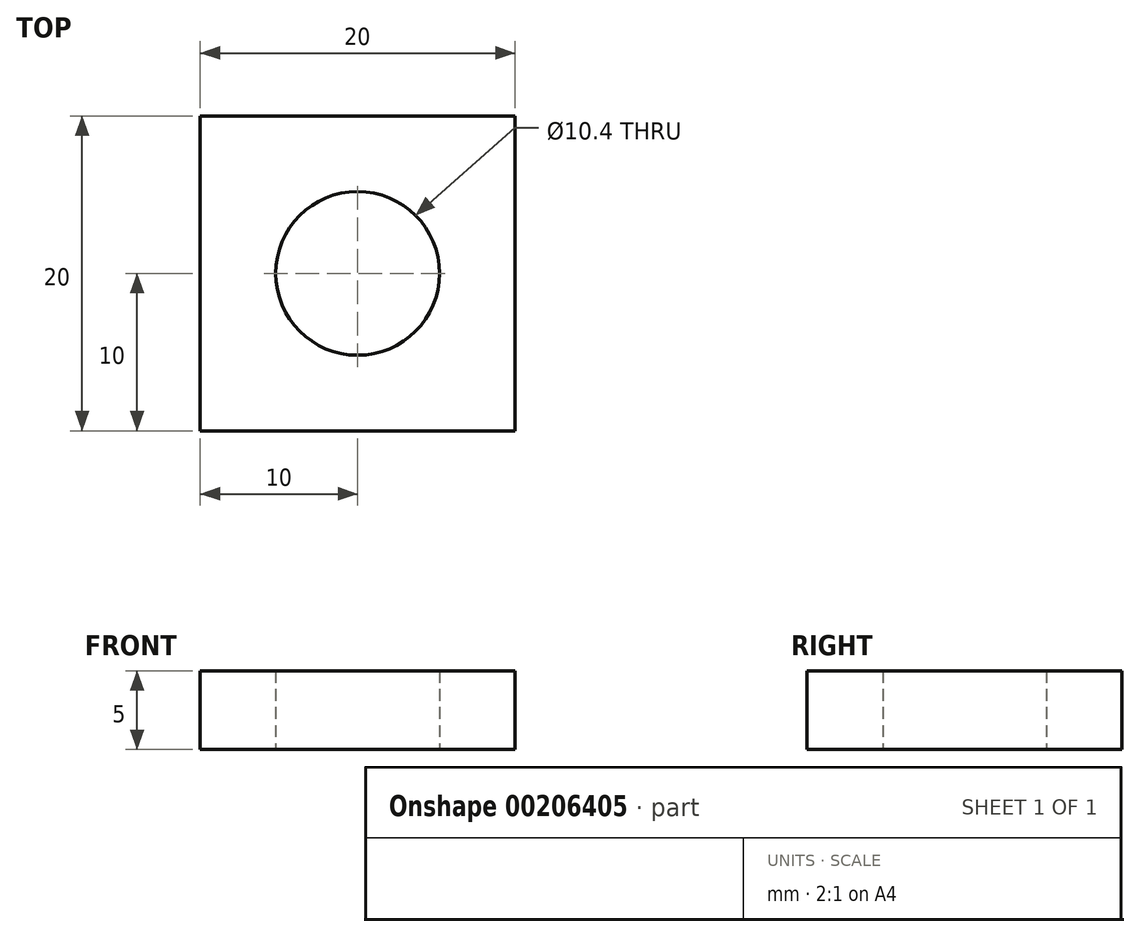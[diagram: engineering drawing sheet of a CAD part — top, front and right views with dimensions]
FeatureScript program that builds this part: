
annotation { "Feature Type Name" : "Feature", "Feature Type Description" : "" }
export const myFeature = defineFeature(function(context is Context, id is Id, definition is map)
    precondition{}
    {
        {
            var Q0;
            Q0=qCreatedBy(makeId("Top.planeOp"),FACE);
            var sketch = newSketch(context, id + "F0", { "sketchPlane" : qUnion([Q0])});
            skCircle(sketch, "E0", {"center": v(0, 0) * mm, "radius": 5.2 * mm});
            skLineSegment(sketch, "E1.bottom", {"start": v(-10, 10) * mm, "end": v(10, 10) * mm});
            skLineSegment(sketch, "E1.top", {"start": v(-10, -10) * mm, "end": v(10, -10) * mm});
            skLineSegment(sketch, "E1.left", {"start": v(-10, 10) * mm, "end": v(-10, -10) * mm});
            skLineSegment(sketch, "E1.right", {"start": v(10, 10) * mm, "end": v(10, -10) * mm});
            skSolve(sketch);
        }
        {
            var Q0;
            Q0 = qSketchRegion(id + "F0", true);
            extrude(context, id + "F1", {"entities" : qUnion([Q0]), "depth" : 5 * mm});
        }
    });
